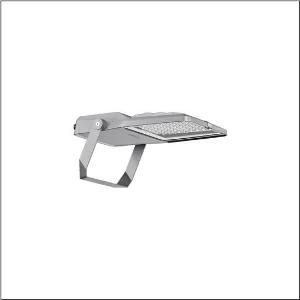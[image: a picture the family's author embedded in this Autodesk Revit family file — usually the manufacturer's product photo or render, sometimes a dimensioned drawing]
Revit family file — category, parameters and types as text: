
# Revit family: floodlight_fl_21_iq_mini___pl33t_5xa7772d4f1a_39e2
name_source: partatom
category: Lighting Fixtures
units: mm (PartAtom-declared; Revit-internal decimal feet)

## family parameters
Cut with Voids When Loaded = No
Host = Face
Light Source = No
Part Type = Normal
Room Calculation Point = No
Round Connector Dimension = Use Diameter
Shared = No

## types (1)
- --- (1 x LED, 18390 lm, 143 W, 4000K)
    Apparent Load = 143 VA
    CIE Flux Codes = 26 75 99 100 100
    Color Rendering = 70
    Color Temperature = 4000K
    Default Elevation = 1800 mm
    Description = Floodlight FL 21 iQ mini, floodlight, primary light control with lens, of PMMA, primary optical cover: protective disc, of toughened safety glass, transparent, light distribution: PL33T, light emission: direct distribution, installation type: surface-mounted, LED, High Power LED, rated luminous flux: 18.390lm, luminous efficacy: 129lm/W, light colour: 740, colour temperature: 4000K, control: Street-Remote, Auto-Match, Temp-Guard, Night-Set, Smart-Wire, Desk-Remote (wireless, voltage-free reading and setting of iQ features in the workshop via application-optimized NFC function/RFID function), optimised constant luminous flux control (CLO 2.0), with terminal, 6-pole, mains connection: 220..240V, AC, 50/60Hz, start of lifetime: 143W, end of service life: 152W, reduction: 61W, luminaire housing, of diecast aluminium, powder-coated, Siteco® metallic grey (DB 702S), corrosivity category C5 mid according to DIN EN ISO 12944, sealing non-destructively replaceable, mounting bracket, of steel, galvanised, powder-coated, Siteco® metallic grey (DB 702S), protection rating (complete): IP66, insulation class (complete): insulation class II (safety insulation), certification: CE, ENEC, VDE, protection symbol: D, impact resistance: IK08, permissible operating ambient temperature: -40..+40°C, permissible operating ambient temperature for outdoor applications: -40..+50°C, standard: DIN EN 12944, LABS conformity tested according to VDMA 24364:2018-05, packaging unit: 1 piece

Light Distribution: PL33T
    Height = 70 mm
    Lamp = 1 x LED
    Lamp Light Flux = 18390 lm
    Lamp Power = 143 W
    Lamp count = 1
    Length = 485 mm
    Luminous efficacy = 129 lm/W
    Manufacturer = Siteco
    ModVariant = No
    Model = 5XA7772D4F1A
    Number of Poles = 1
    OnlyDefault = Yes
    Power Factor = 1
    Product Name = Floodlight FL 21 iQ mini | PL33T
    Product group = floodlight | pylon annexe
    ProductGroupID = 6200
    Protection Class = Protection class II
    Protection Degree = IP 66
    RLX_Detail_Level = 1
    RLX_Emergency_Light_Flux = 0 lm
    RLX_Emergency_Type = 0
    RLX_Emergency_Type_DB = No
    RlxData = <blob elided: 96465 chars, md5=3e9b44e5>
    Socket = socket
    Standby Power = 0 W
    System Light Flux = 18390 lm
    System Power = 143 W
    Type Comments = factory setting: luminous flux: 100 % | dim-lin: 254 | 730 mA
    Type Image = l_1006845.jpg
    URL = http://relux.com
    VarID = @adj_099013
    Voltage = 0 V
    Weight = 0.00 kg
    Width = 337 mm

## geometry (parser evidence)
native form markers: Blend x4, Sweep x13
no freeform markers — native parametric forms only
